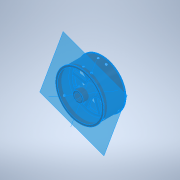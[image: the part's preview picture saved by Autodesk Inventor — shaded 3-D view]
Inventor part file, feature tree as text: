
AUTODESK INVENTOR PART (.ipt)
format: ipt  version: 2020 (Build 240168000, 168)  size: 322,048 bytes
history: native  units: in
note: dims shown in document units (in); Inventor stores cm internally (conversion verified against a paired STEP export)
features: sketch x2, plane x2, extrude x1, pattern_circular x1
ambient origin geometry x8: Origin, YZ Plane, XZ Plane, XY Plane, X Axis, Y Axis, Z Axis, Center Point
bodies: Solid1 (feature_tree)
feature tree (6):
  extrude  "Extrusion1"  Depth=1.0in TaperAngle=0.0deg
  sketch  "Sketch3"  dims[d15=0.47in d16=1.1811in d18=0.0in d20=1.1811in d22=0.0in d27=120.0deg d28=120.0deg d29=0.6184in d30=0.6184in d31=0.1in d32=0.4992in d33=3.5203in d34=3.7699in d35=3.5203in d36=3.6in]
  plane  "Work Plane2"
  plane  "Work Plane3"
  sketch  "Sketch2"  dims[d9=1.0in d10=0.0in d11=1.1811in d13=0.0in]
  pattern_circular  "CirPattern3"
